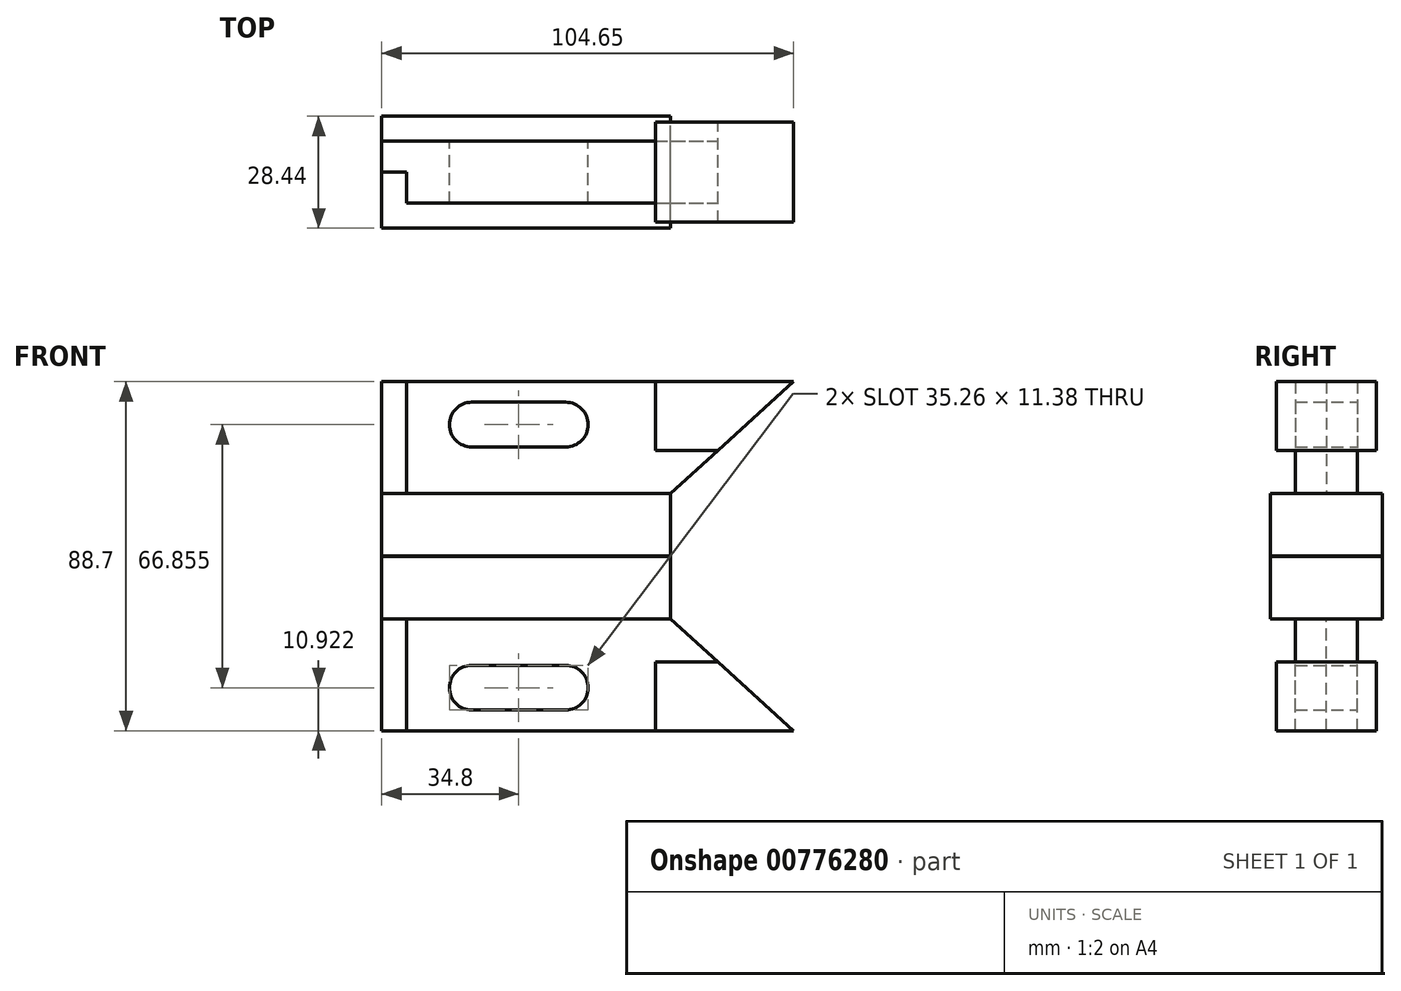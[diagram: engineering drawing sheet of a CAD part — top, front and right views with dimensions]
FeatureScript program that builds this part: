
annotation { "Feature Type Name" : "Feature", "Feature Type Description" : "" }
export const myFeature = defineFeature(function(context is Context, id is Id, definition is map)
    precondition{}
    {
        {
            var Q0;
            Q0=qCreatedBy(makeId("Front.planeOp"),FACE);
            var sketch = newSketch(context, id + "F0", { "sketchPlane" : qUnion([Q0])});
            skLineSegment(sketch, "E0", {"start": v(-68.39, 44.35) * mm, "end": v(36.26, 44.35) * mm});
            skLineSegment(sketch, "E1", {"start": v(-68.39, 44.35) * mm, "end": v(-68.39, 15.9) * mm});
            skLineSegment(sketch, "E2", {"start": v(-68.39, 44.35) * mm, "end": v(1.2, 44.35) * mm});
            skLineSegment(sketch, "E3", {"start": v(1.2, 44.35) * mm, "end": v(1.2, 26.82) * mm});
            skLineSegment(sketch, "E4", {"start": v(-68.39, 15.9) * mm, "end": v(5.02, 15.9) * mm});
            skLineSegment(sketch, "E5", {"start": v(5.02, 15.9) * mm, "end": v(36.26, 44.35) * mm});
            skLineSegment(sketch, "E6", {"start": v(1.2, 26.82) * mm, "end": v(17.01, 26.82) * mm});
            skLineSegment(sketch, "E7", {"start": v(-68.39, 15.9) * mm, "end": v(-68.39, 33.43) * mm});
            skLineSegment(sketch, "E8", {"start": v(-68.39, 33.43) * mm, "end": v(1.2, 33.43) * mm, "construction": true});
            skPoint(sketch, "E9.middle", {"position": v(-33.59, 33.43) * mm});
            skPoint(sketch, "E10.orphan", {"position": v(-47, 28.01) * mm});
            skPoint(sketch, "E11.orphan", {"position": v(-39.92, 39.12) * mm});
            skPoint(sketch, "E12.orphan", {"position": v(-20.19, 38.84) * mm});
            skPoint(sketch, "E13.orphan", {"position": v(-27.26, 27.74) * mm});
            skLineSegment(sketch, "E14.bottom", {"start": v(-21.65, 27.74) * mm, "end": v(-45.53, 27.74) * mm});
            skLineSegment(sketch, "E14.top", {"start": v(-21.65, 39.12) * mm, "end": v(-45.53, 39.12) * mm});
            skArc(sketch, "E15", {"start": v(-45.53, 39.12) * mm, "mid": v(-51.22, 33.43) * mm, "end": v(-45.53, 27.74) * mm});
            skArc(sketch, "E16", {"start": v(-21.65, 27.74) * mm, "mid": v(-15.96, 33.43) * mm, "end": v(-21.65, 39.12) * mm});
            skPoint(sketch, "E17.orphan", {"position": v(-51.44, 27.74) * mm});
            skPoint(sketch, "E18.orphan", {"position": v(-51.44, 39.12) * mm});
            skPoint(sketch, "E19.orphan", {"position": v(-15.74, 39.12) * mm});
            skPoint(sketch, "E20.orphan", {"position": v(-15.74, 27.74) * mm});
            skLineSegment(sketch, "E21", {"start": v(-68.39, 44.35) * mm, "end": v(-62.04, 44.35) * mm, "construction": true});
            skLineSegment(sketch, "E22", {"start": v(-62.04, 44.35) * mm, "end": v(-62.04, 15.9) * mm});
            skLineSegment(sketch, "E23", {"start": v(-62.04, 15.9) * mm, "end": v(-68.39, 15.9) * mm});
            skLineSegment(sketch, "E24", {"start": v(-68.39, 44.35) * mm, "end": v(-68.39, -0.1) * mm, "construction": true});
            skLineSegment(sketch, "E25", {"start": v(-68.39, 44.35) * mm, "end": v(-68.39, -0.1) * mm});
            skLineSegment(sketch, "E26", {"start": v(-68.39, -0.1) * mm, "end": v(5.02, -0.1) * mm});
            skLineSegment(sketch, "E27", {"start": v(5.02, 15.9) * mm, "end": v(5.02, -0.1) * mm});
            skSolve(sketch);
        }
        {
            var Q0;
            Q0=makeQuery(id+"F0.imprint","IMPRINT",FACE,{"disambiguationData":[TD([[makeQuery(id+"F0.imprint","IMPRINT",EDGE,{"derivedFrom":sQuery(id+"F0.wireOp",EDGE,"E4")}),-1.0]])]});
            extrude(context, id + "F1", {"entities" : qUnion([Q0]), "depth" : 28.45 * mm, "offsetDistance" : 25.4 * mm});
        }
        {
            var Q0;
            {var subQ0=sQuery(id+"F0.wireOp",EDGE,"E0");Q0=makeQuery(id+"F0.imprint","IMPRINT",FACE,{"disambiguationData":[TD([[makeQuery(id+"F0.imprint","IMPRINT",EDGE,{"derivedFrom":subQ0}),-1.0]])]});}
            extrude(context, id + "F2", {"entities" : qUnion([Q0]), "depth" : 25.4 * mm, "offsetDistance" : 25.4 * mm, "symmetric" : true});
        }
        {
            var Q0;
            {var subQ3=sQuery(id+"F0.wireOp",EDGE,"E3");Q0=makeQuery(id+"F0.imprint","IMPRINT",FACE,{"disambiguationData":[TD([[makeQuery(id+"F0.imprint","IMPRINT",EDGE,{"derivedFrom":subQ3}),-1.0]])]});}
            extrude(context, id + "F3", {"entities" : qUnion([Q0]), "depth" : 15.75 * mm, "offsetDistance" : 25.4 * mm, "symmetric" : true});
        }
        {
            var Q0;
            Q0=makeQuery(id+"F1.opExtrude","CAP_FACE",FACE,{"disambiguationData":[OSD([sQuery(id+"F0.wireOp",EDGE,"E4"),sQuery(id+"F0.wireOp",EDGE,"E23"),sQuery(id+"F0.wireOp",EDGE,"E25"),sQuery(id+"F0.wireOp",EDGE,"E26"),sQuery(id+"F0.wireOp",EDGE,"E27")])],"isStart":false});
            extrude(context, id + "F4", {"entities" : qUnion([Q0]), "operationType" : NewBodyOperationType.REMOVE, "oppositeDirection" : true, "depth" : 28.45 * mm, "offsetDistance" : 25.4 * mm});
        }
        {
            var Q0;
            Q0=makeQuery(id+"F0.imprint","IMPRINT",FACE,{"disambiguationData":[TD([[makeQuery(id+"F0.imprint","IMPRINT",EDGE,{"derivedFrom":sQuery(id+"F0.wireOp",EDGE,"E4")}),-1.0]])]});
            extrude(context, id + "F5", {"entities" : qUnion([Q0]), "operationType" : NewBodyOperationType.ADD, "depth" : 28.45 * mm, "offsetDistance" : 25.4 * mm, "symmetric" : true});
        }
        {
            var Q0;
            {var subQ3=sQuery(id+"F0.wireOp",EDGE,"E22");Q0=makeQuery(id+"F0.imprint","IMPRINT",FACE,{"disambiguationData":[TD([[makeQuery(id+"F0.imprint","IMPRINT",EDGE,{"derivedFrom":subQ3}),-1.0]])]});}
            extrude(context, id + "F6", {"entities" : qUnion([Q0]), "operationType" : NewBodyOperationType.ADD, "oppositeDirection" : true, "depth" : 7.87 * mm, "offsetDistance" : 25.4 * mm});
        }
        {
            var Q0;
            Q0=makeQuery(id+"F2.opExtrude","SWEPT_BODY",BODY,{"disambiguationData":[OSD([sQuery(id+"F0.wireOp",EDGE,"E0"),sQuery(id+"F0.wireOp",EDGE,"E3"),sQuery(id+"F0.wireOp",EDGE,"E5"),sQuery(id+"F0.wireOp",EDGE,"E6")])]});
            var Q1;
            Q1=makeQuery(id+"F3.opExtrude","SWEPT_BODY",BODY,{"disambiguationData":[OSD([sQuery(id+"F0.wireOp",EDGE,"E2"),sQuery(id+"F0.wireOp",EDGE,"E3"),sQuery(id+"F0.wireOp",EDGE,"E4"),sQuery(id+"F0.wireOp",EDGE,"E5"),sQuery(id+"F0.wireOp",EDGE,"E6"),sQuery(id+"F0.wireOp",EDGE,"E14.bottom"),sQuery(id+"F0.wireOp",EDGE,"E14.top"),sQuery(id+"F0.wireOp",EDGE,"E15"),sQuery(id+"F0.wireOp",EDGE,"E16"),sQuery(id+"F0.wireOp",EDGE,"E22")])]});
            var Q2;
            Q2=qCreatedBy(makeId("Top.planeOp"),FACE);
            mirror(context, id + "F7", {"entities" : qUnion([Q0, Q1]), "mirrorPlane" : qUnion([Q2])});
        }
    });
